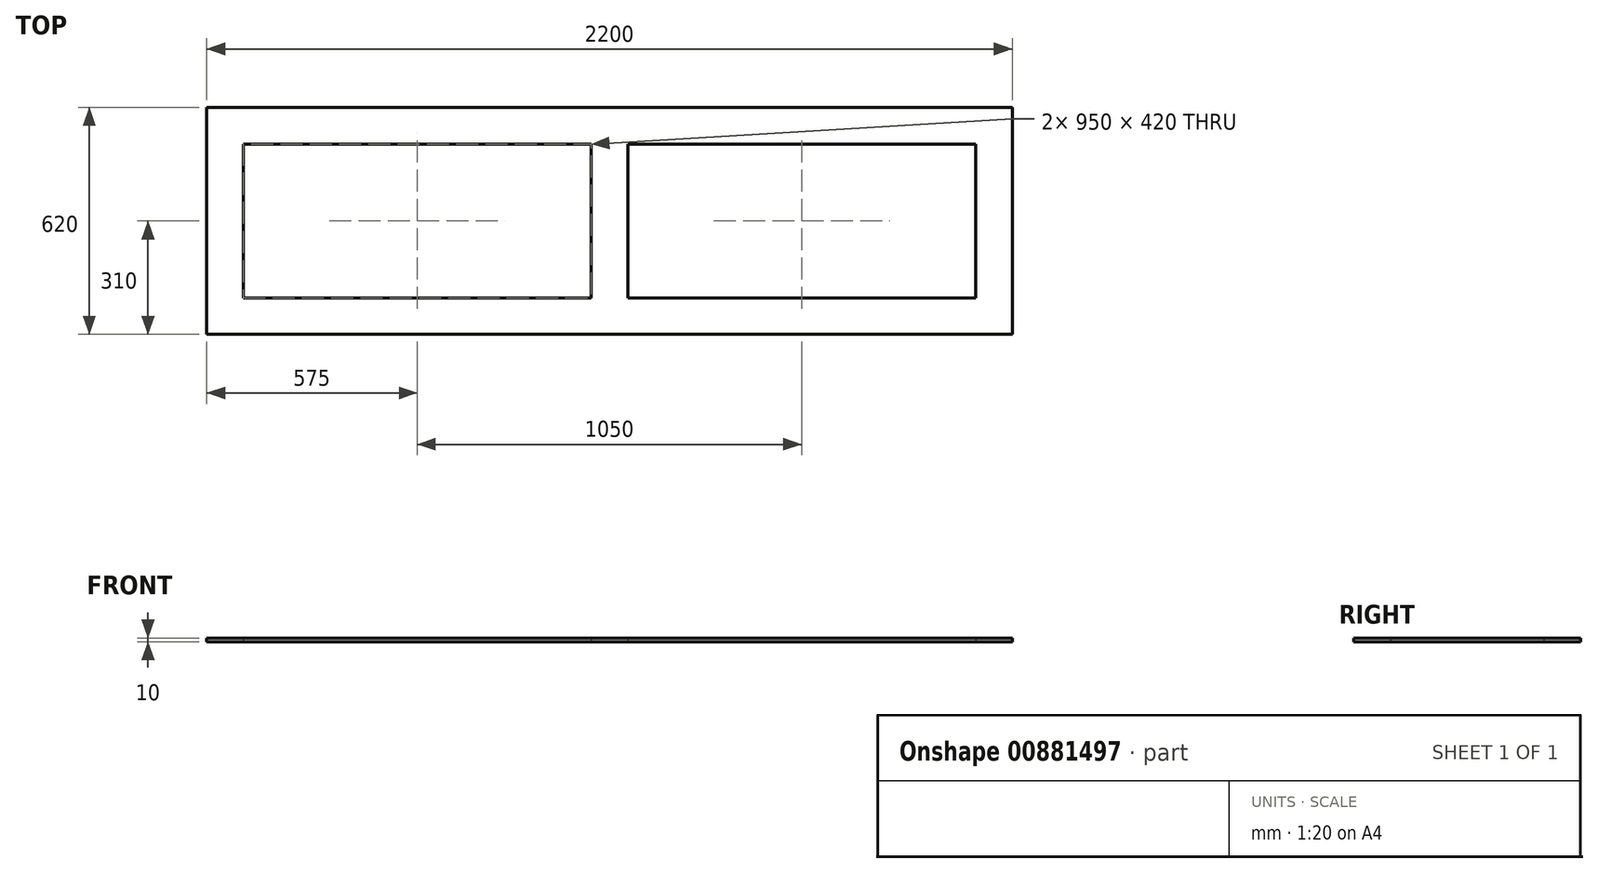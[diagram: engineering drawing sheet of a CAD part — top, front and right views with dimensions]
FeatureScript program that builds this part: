
annotation { "Feature Type Name" : "Feature", "Feature Type Description" : "" }
export const myFeature = defineFeature(function(context is Context, id is Id, definition is map)
    precondition{}
    {
        {
            var Q0;
            Q0=qCreatedBy(makeId("Top.planeOp"),FACE);
            var sketch = newSketch(context, id + "F0", { "sketchPlane" : qUnion([Q0])});
            skLineSegment(sketch, "E0.bottom", {"start": v(1100, 310) * mm, "end": v(-1100, 310) * mm});
            skLineSegment(sketch, "E0.top", {"start": v(1100, -310) * mm, "end": v(-1100, -310) * mm});
            skLineSegment(sketch, "E0.left", {"start": v(1100, 310) * mm, "end": v(1100, -310) * mm});
            skLineSegment(sketch, "E0.right", {"start": v(-1100, 310) * mm, "end": v(-1100, -310) * mm});
            skPoint(sketch, "E0.middle", {"position": v(0, 0) * mm});
            skLineSegment(sketch, "E1.bottom", {"start": v(-1000, 210) * mm, "end": v(-50, 210) * mm});
            skLineSegment(sketch, "E1.top", {"start": v(-1000, -210) * mm, "end": v(-50, -210) * mm});
            skLineSegment(sketch, "E1.left", {"start": v(-1000, 210) * mm, "end": v(-1000, -210) * mm});
            skLineSegment(sketch, "E1.right", {"start": v(-50, 210) * mm, "end": v(-50, -210) * mm});
            skLineSegment(sketch, "E2.bottom", {"start": v(50, 210) * mm, "end": v(1000, 210) * mm});
            skLineSegment(sketch, "E2.top", {"start": v(50, -210) * mm, "end": v(1000, -210) * mm});
            skLineSegment(sketch, "E2.left", {"start": v(50, 210) * mm, "end": v(50, -210) * mm});
            skLineSegment(sketch, "E2.right", {"start": v(1000, 210) * mm, "end": v(1000, -210) * mm});
            skLineSegment(sketch, "E3", {"start": v(0, 310) * mm, "end": v(0, -310) * mm, "construction": true});
            skSolve(sketch);
        }
        {
            var Q0;
            Q0 = qSketchRegion(id + "F0", true);
            extrude(context, id + "F1", {"entities" : qUnion([Q0]), "depth" : 10 * mm, "offsetDistance" : 25 * mm});
        }
    });
